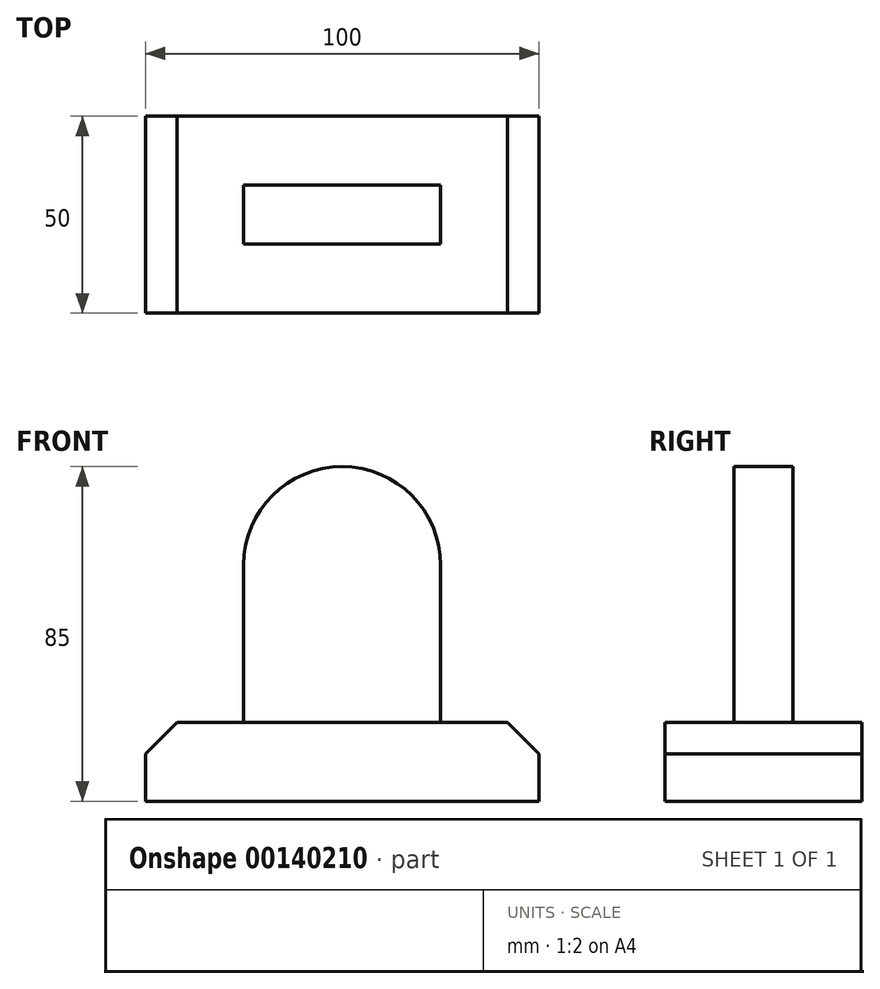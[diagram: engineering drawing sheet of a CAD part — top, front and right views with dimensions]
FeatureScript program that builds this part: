
annotation { "Feature Type Name" : "Feature", "Feature Type Description" : "" }
export const myFeature = defineFeature(function(context is Context, id is Id, definition is map)
    precondition{}
    {
        {
            var Q0;
            Q0=qCreatedBy(makeId("Top.planeOp"),FACE);
            var sketch = newSketch(context, id + "F0", { "sketchPlane" : qUnion([Q0])});
            skLineSegment(sketch, "E0.bottom", {"start": v(-50, -25) * mm, "end": v(50, -25) * mm});
            skLineSegment(sketch, "E0.top", {"start": v(-50, 25) * mm, "end": v(50, 25) * mm});
            skLineSegment(sketch, "E0.left", {"start": v(-50, -25) * mm, "end": v(-50, 25) * mm});
            skLineSegment(sketch, "E0.right", {"start": v(50, -25) * mm, "end": v(50, 25) * mm});
            skPoint(sketch, "E0.middle", {"position": v(0, 0) * mm});
            skSolve(sketch);
        }
        {
            var Q0;
            Q0=makeQuery(id+"F0.imprint","IMPRINT",FACE,{"disambiguationData":[TD([[makeQuery(id+"F0.imprint","IMPRINT",EDGE,{"derivedFrom":sQuery(id+"F0.wireOp",EDGE,"E0.bottom")}),1.0]])]});
            extrude(context, id + "F1", {"entities" : qUnion([Q0]), "depth" : 20 * mm});
        }
        {
            var Q0;
            Q0=makeQuery(id+"F1.opExtrude","CAP_EDGE",EDGE,{"disambiguationData":[OSD([sQuery(id+"F0.wireOp",EDGE,"E0.left")])],"isStart":false});
            var Q1;
            Q1=makeQuery(id+"F1.opExtrude","CAP_EDGE",EDGE,{"disambiguationData":[OSD([sQuery(id+"F0.wireOp",EDGE,"E0.right")])],"isStart":false});
            chamfer(context, id + "F2", {"entities" : qUnion([Q0, Q1]), "width" : 8 * mm, "tangentPropagation" : true});
        }
        {
            var Q0;
            Q0=qCreatedBy(makeId("Front.planeOp"),FACE);
            var sketch = newSketch(context, id + "F3", { "sketchPlane" : qUnion([Q0])});
            skLineSegment(sketch, "E1", {"start": v(-25, 20) * mm, "end": v(-25, 60) * mm});
            skArc(sketch, "E2", {"start": v(25, 60) * mm, "mid": v(0, 85) * mm, "end": v(-25, 60) * mm});
            skLineSegment(sketch, "E3", {"start": v(25, 60) * mm, "end": v(25, 20) * mm});
            skLineSegment(sketch, "E4", {"start": v(-25, 20) * mm, "end": v(25, 20) * mm});
            skSolve(sketch);
        }
        {
            var Q0;
            Q0=makeQuery(id+"F3.imprint","IMPRINT",FACE,{"disambiguationData":[TD([[makeQuery(id+"F3.imprint","IMPRINT",EDGE,{"derivedFrom":sQuery(id+"F3.wireOp",EDGE,"E1")}),-1.0]])]});
            extrude(context, id + "F4", {"entities" : qUnion([Q0]), "operationType" : NewBodyOperationType.ADD, "endBound" : BoundingType.SYMMETRIC, "depth" : 15 * mm});
        }
    });
